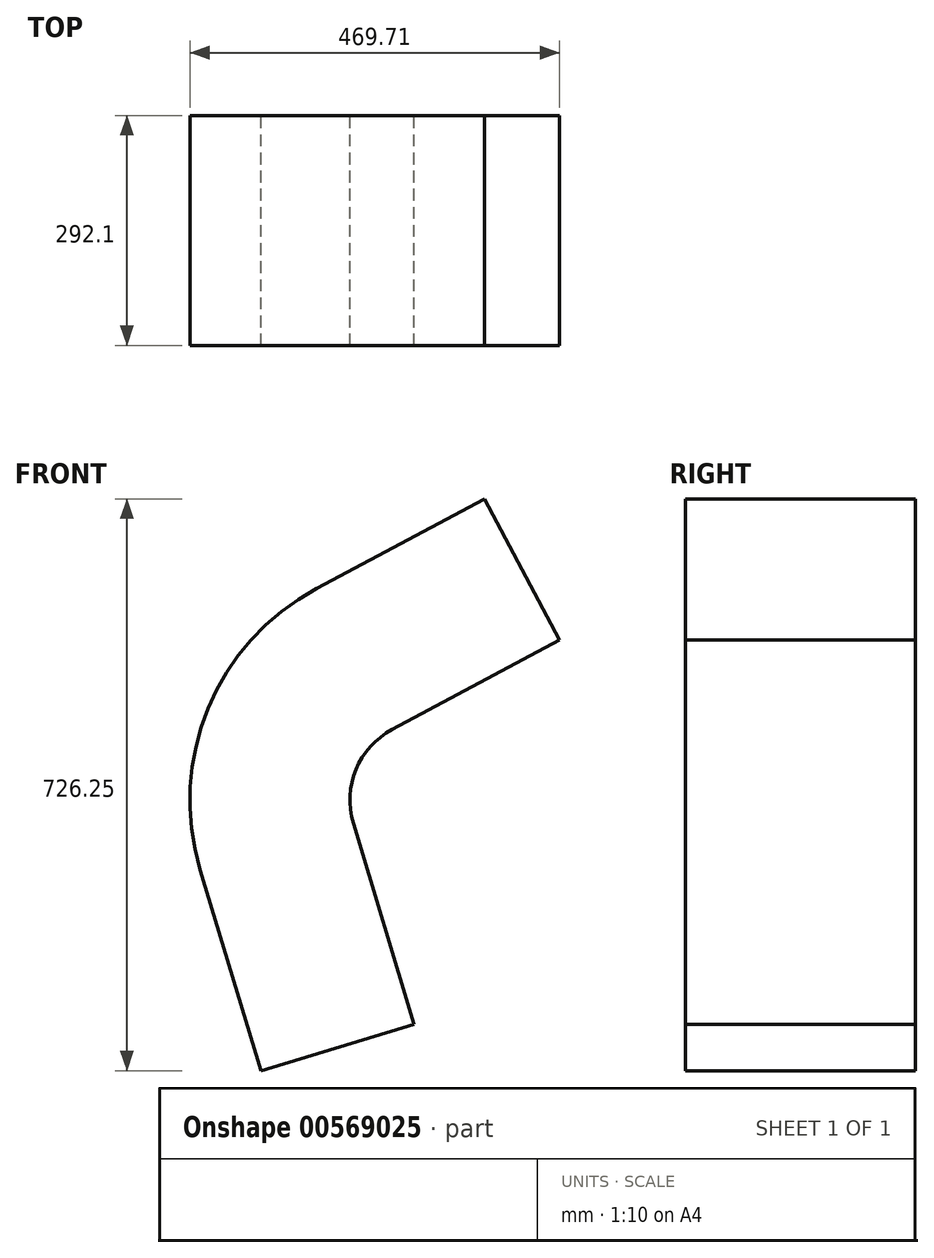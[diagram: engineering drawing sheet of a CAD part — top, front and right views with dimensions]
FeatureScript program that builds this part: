
annotation { "Feature Type Name" : "Feature", "Feature Type Description" : "" }
export const myFeature = defineFeature(function(context is Context, id is Id, definition is map)
    precondition{}
    {
        {
            var Q0;
            Q0=qCreatedBy(makeId("Front.planeOp"),FACE);
            var sketch = newSketch(context, id + "F0", { "sketchPlane" : qUnion([Q0])});
            skCircle(sketch, "E0", {"center": v(0, 0) * mm, "radius": 304.8 * mm});
            skPoint(sketch, "E1.end.orphan", {"position": v(215.53, -215.53) * mm});
            skPoint(sketch, "E2.end.orphan", {"position": v(-215.53, -215.53) * mm});
            skLineSegment(sketch, "E3", {"start": v(0, 0) * mm, "end": v(-281.6, 116.64) * mm});
            skLineSegment(sketch, "E4", {"start": v(0, 0) * mm, "end": v(-298.94, 59.46) * mm});
            skLineSegment(sketch, "E5", {"start": v(0, 0) * mm, "end": v(-291.68, 88.48) * mm});
            skLineSegment(sketch, "E6.MirrorCS", {"start": v(0, 0) * mm, "end": v(-268.8, 143.68) * mm});
            skLineSegment(sketch, "E7.MirrorCS", {"start": v(0, 0) * mm, "end": v(-253.43, 169.34) * mm});
            skLineSegment(sketch, "E8.MirrorCS", {"start": v(0, 0) * mm, "end": v(-235.61, 193.36) * mm});
            skLineSegment(sketch, "E9.MirrorCS", {"start": v(0, 0) * mm, "end": v(-215.53, 215.53) * mm});
            skLineSegment(sketch, "E10.MirrorCS", {"start": v(0, 0) * mm, "end": v(-193.36, 235.61) * mm});
            skLineSegment(sketch, "E11.MirrorCS", {"start": v(0, 0) * mm, "end": v(-169.34, 253.43) * mm});
            skLineSegment(sketch, "E12.MirrorCS", {"start": v(0, 0) * mm, "end": v(-143.68, 268.8) * mm});
            skLineSegment(sketch, "E13.MirrorCS", {"start": v(0, 0) * mm, "end": v(-116.64, 281.6) * mm});
            skLineSegment(sketch, "E14.MirrorCS", {"start": v(0, 0) * mm, "end": v(-88.48, 291.68) * mm});
            skLineSegment(sketch, "E15.MirrorCS", {"start": v(0, 0) * mm, "end": v(-59.46, 298.94) * mm});
            skLineSegment(sketch, "E16.MirrorCS", {"start": v(0, 0) * mm, "end": v(-29.88, 303.33) * mm});
            skLineSegment(sketch, "E17.MirrorCS", {"start": v(0, 0) * mm, "end": v(0, 304.8) * mm});
            skLineSegment(sketch, "E18.MirrorCS", {"start": v(0, 0) * mm, "end": v(29.88, 303.33) * mm});
            skLineSegment(sketch, "E19.MirrorCS", {"start": v(0, 0) * mm, "end": v(59.46, 298.94) * mm});
            skLineSegment(sketch, "E20.MirrorCS", {"start": v(0, 0) * mm, "end": v(88.48, 291.68) * mm});
            skLineSegment(sketch, "E21.MirrorCS", {"start": v(0, 0) * mm, "end": v(116.64, 281.6) * mm});
            skLineSegment(sketch, "E22.MirrorCS", {"start": v(0, 0) * mm, "end": v(143.68, 268.8) * mm});
            skLineSegment(sketch, "E23.MirrorCS", {"start": v(0, 0) * mm, "end": v(169.34, 253.43) * mm});
            skLineSegment(sketch, "E24.MirrorCS", {"start": v(0, 0) * mm, "end": v(193.36, 235.61) * mm});
            skLineSegment(sketch, "E25.MirrorCS", {"start": v(0, 0) * mm, "end": v(215.53, 215.53) * mm});
            skLineSegment(sketch, "E26.MirrorCS", {"start": v(0, 0) * mm, "end": v(235.61, 193.36) * mm});
            skLineSegment(sketch, "E27.MirrorCS", {"start": v(0, 0) * mm, "end": v(253.43, 169.34) * mm});
            skLineSegment(sketch, "E28.MirrorCS", {"start": v(0, 0) * mm, "end": v(268.8, 143.68) * mm});
            skLineSegment(sketch, "E29.MirrorCS", {"start": v(0, 0) * mm, "end": v(281.6, 116.64) * mm});
            skLineSegment(sketch, "E30.MirrorCS", {"start": v(0, 0) * mm, "end": v(291.68, 88.48) * mm});
            skLineSegment(sketch, "E31.MirrorCS", {"start": v(0, 0) * mm, "end": v(298.94, 59.46) * mm});
            skLineSegment(sketch, "E32.MirrorCS", {"start": v(0, 0) * mm, "end": v(303.33, 29.88) * mm});
            skLineSegment(sketch, "E33.MirrorCS", {"start": v(0, 0) * mm, "end": v(304.8, 0) * mm});
            skLineSegment(sketch, "E34.MirrorCS", {"start": v(0, 0) * mm, "end": v(303.33, -29.88) * mm});
            skLineSegment(sketch, "E35.MirrorCS", {"start": v(0, 0) * mm, "end": v(298.94, -59.46) * mm});
            skLineSegment(sketch, "E36.MirrorCS", {"start": v(0, 0) * mm, "end": v(291.68, -88.48) * mm});
            skLineSegment(sketch, "E37.MirrorCS", {"start": v(0, 0) * mm, "end": v(281.6, -116.64) * mm});
            skLineSegment(sketch, "E38.MirrorCS", {"start": v(0, 0) * mm, "end": v(268.8, -143.68) * mm});
            skLineSegment(sketch, "E39.MirrorCS", {"start": v(0, 0) * mm, "end": v(253.43, -169.34) * mm});
            skLineSegment(sketch, "E40.MirrorCS", {"start": v(0, 0) * mm, "end": v(235.61, -193.36) * mm});
            skLineSegment(sketch, "E41.MirrorCS", {"start": v(0, 0) * mm, "end": v(215.53, -215.53) * mm});
            skLineSegment(sketch, "E42.MirrorCS", {"start": v(0, 0) * mm, "end": v(193.36, -235.61) * mm});
            skLineSegment(sketch, "E43.MirrorCS", {"start": v(0, 0) * mm, "end": v(169.34, -253.43) * mm});
            skLineSegment(sketch, "E44.MirrorCS", {"start": v(0, 0) * mm, "end": v(143.68, -268.8) * mm});
            skLineSegment(sketch, "E45.MirrorCS", {"start": v(0, 0) * mm, "end": v(116.64, -281.6) * mm});
            skLineSegment(sketch, "E46.MirrorCS", {"start": v(0, 0) * mm, "end": v(88.48, -291.68) * mm});
            skLineSegment(sketch, "E47.MirrorCS", {"start": v(0, 0) * mm, "end": v(59.46, -298.94) * mm});
            skLineSegment(sketch, "E48.MirrorCS", {"start": v(0, 0) * mm, "end": v(29.88, -303.33) * mm});
            skLineSegment(sketch, "E49.MirrorCS", {"start": v(0, 0) * mm, "end": v(0, -304.8) * mm});
            skLineSegment(sketch, "E50.MirrorCS", {"start": v(0, 0) * mm, "end": v(-29.88, -303.33) * mm});
            skLineSegment(sketch, "E51.MirrorCS", {"start": v(0, 0) * mm, "end": v(-59.46, -298.94) * mm});
            skLineSegment(sketch, "E52.MirrorCS", {"start": v(0, 0) * mm, "end": v(-88.48, -291.68) * mm});
            skLineSegment(sketch, "E53.MirrorCS", {"start": v(0, 0) * mm, "end": v(-116.64, -281.6) * mm});
            skLineSegment(sketch, "E54.MirrorCS", {"start": v(0, 0) * mm, "end": v(-143.68, -268.8) * mm});
            skLineSegment(sketch, "E55.MirrorCS", {"start": v(0, 0) * mm, "end": v(-169.34, -253.43) * mm});
            skLineSegment(sketch, "E56.MirrorCS", {"start": v(0, 0) * mm, "end": v(-193.36, -235.61) * mm});
            skLineSegment(sketch, "E57.MirrorCS", {"start": v(0, 0) * mm, "end": v(-215.53, -215.53) * mm});
            skLineSegment(sketch, "E58.MirrorCS", {"start": v(0, 0) * mm, "end": v(-235.61, -193.36) * mm});
            skLineSegment(sketch, "E59.MirrorCS", {"start": v(0, 0) * mm, "end": v(-253.43, -169.34) * mm});
            skLineSegment(sketch, "E60.MirrorCS", {"start": v(0, 0) * mm, "end": v(-268.8, -143.68) * mm});
            skLineSegment(sketch, "E61.MirrorCS", {"start": v(0, 0) * mm, "end": v(-281.6, -116.64) * mm});
            skLineSegment(sketch, "E62.MirrorCS", {"start": v(0, 0) * mm, "end": v(-291.68, -88.48) * mm});
            skLineSegment(sketch, "E63.MirrorCS", {"start": v(0, 0) * mm, "end": v(-303.33, -29.88) * mm});
            skLineSegment(sketch, "E64.MirrorCS", {"start": v(0, 0) * mm, "end": v(-298.94, -59.46) * mm});
            skLineSegment(sketch, "E65.MirrorCS", {"start": v(0, 0) * mm, "end": v(-304.8, 0) * mm});
            skLineSegment(sketch, "E66.MirrorCS", {"start": v(0, 0) * mm, "end": v(-303.33, 29.88) * mm});
            skCircle(sketch, "E67", {"center": v(0, 0) * mm, "radius": 317.5 * mm});
            skCircle(sketch, "E68", {"center": v(0, 0) * mm, "radius": 101.6 * mm});
            skSolve(sketch);
        }
        {
            var Q0;
            {var subQ0=sQuery(id+"F0.wireOp",EDGE,"E12.MirrorCS");var subQ1=sQuery(id+"F0.wireOp",EDGE,"E0");var subQ2=makeQuery(id+"F0.imprint","INTERSECT",VERTEX,{"derivedFrom":[subQ1,subQ0]});Q0=makeQuery(id+"F0.imprint","IMPRINT",FACE,{"disambiguationData":[TD([[makeQuery(id+"F0.imprint","IMPRINT",EDGE,{"disambiguationData":[TD([[subQ2,-1.0]])],"derivedFrom":subQ1}),1.0]])]});}
            var Q1;
            {var subQ0=sQuery(id+"F0.wireOp",EDGE,"E66.MirrorCS");var subQ1=sQuery(id+"F0.wireOp",EDGE,"E0");var subQ2=makeQuery(id+"F0.imprint","INTERSECT",VERTEX,{"derivedFrom":[subQ1,subQ0]});Q1=makeQuery(id+"F0.imprint","IMPRINT",FACE,{"disambiguationData":[TD([[makeQuery(id+"F0.imprint","IMPRINT",EDGE,{"disambiguationData":[TD([[subQ2,-1.0]])],"derivedFrom":subQ1}),1.0]])]});}
            var Q2;
            {var subQ0=sQuery(id+"F0.wireOp",EDGE,"E4");var subQ1=sQuery(id+"F0.wireOp",EDGE,"E0");var subQ2=makeQuery(id+"F0.imprint","INTERSECT",VERTEX,{"derivedFrom":[subQ1,subQ0]});Q2=makeQuery(id+"F0.imprint","IMPRINT",FACE,{"disambiguationData":[TD([[makeQuery(id+"F0.imprint","IMPRINT",EDGE,{"disambiguationData":[TD([[subQ2,-1.0]])],"derivedFrom":subQ1}),1.0]])]});}
            var Q3;
            {var subQ0=sQuery(id+"F0.wireOp",EDGE,"E11.MirrorCS");var subQ1=sQuery(id+"F0.wireOp",EDGE,"E0");var subQ2=makeQuery(id+"F0.imprint","INTERSECT",VERTEX,{"derivedFrom":[subQ1,subQ0]});Q3=makeQuery(id+"F0.imprint","IMPRINT",FACE,{"disambiguationData":[TD([[makeQuery(id+"F0.imprint","IMPRINT",EDGE,{"disambiguationData":[TD([[subQ2,-1.0]])],"derivedFrom":subQ1}),1.0]])]});}
            var Q4;
            {var subQ0=sQuery(id+"F0.wireOp",EDGE,"E65.MirrorCS");var subQ1=sQuery(id+"F0.wireOp",EDGE,"E0");var subQ2=makeQuery(id+"F0.imprint","INTERSECT",VERTEX,{"derivedFrom":[subQ1,subQ0]});Q4=makeQuery(id+"F0.imprint","IMPRINT",FACE,{"disambiguationData":[TD([[makeQuery(id+"F0.imprint","IMPRINT",EDGE,{"disambiguationData":[TD([[subQ2,-1.0]])],"derivedFrom":subQ1}),1.0]])]});}
            var Q5;
            {var subQ0=sQuery(id+"F0.wireOp",EDGE,"E10.MirrorCS");var subQ1=sQuery(id+"F0.wireOp",EDGE,"E0");var subQ2=makeQuery(id+"F0.imprint","INTERSECT",VERTEX,{"derivedFrom":[subQ1,subQ0]});Q5=makeQuery(id+"F0.imprint","IMPRINT",FACE,{"disambiguationData":[TD([[makeQuery(id+"F0.imprint","IMPRINT",EDGE,{"disambiguationData":[TD([[subQ2,-1.0]])],"derivedFrom":subQ1}),1.0]])]});}
            var Q6;
            {var subQ0=sQuery(id+"F0.wireOp",EDGE,"E63.MirrorCS");var subQ1=sQuery(id+"F0.wireOp",EDGE,"E0");var subQ2=makeQuery(id+"F0.imprint","INTERSECT",VERTEX,{"derivedFrom":[subQ1,subQ0]});Q6=makeQuery(id+"F0.imprint","IMPRINT",FACE,{"disambiguationData":[TD([[makeQuery(id+"F0.imprint","IMPRINT",EDGE,{"disambiguationData":[TD([[subQ2,-1.0]])],"derivedFrom":subQ1}),1.0]])]});}
            var Q7;
            {var subQ0=sQuery(id+"F0.wireOp",EDGE,"E9.MirrorCS");var subQ1=sQuery(id+"F0.wireOp",EDGE,"E0");var subQ2=makeQuery(id+"F0.imprint","INTERSECT",VERTEX,{"derivedFrom":[subQ1,subQ0]});Q7=makeQuery(id+"F0.imprint","IMPRINT",FACE,{"disambiguationData":[TD([[makeQuery(id+"F0.imprint","IMPRINT",EDGE,{"disambiguationData":[TD([[subQ2,-1.0]])],"derivedFrom":subQ1}),1.0]])]});}
            var Q8;
            {var subQ0=sQuery(id+"F0.wireOp",EDGE,"E64.MirrorCS");var subQ1=sQuery(id+"F0.wireOp",EDGE,"E0");var subQ2=makeQuery(id+"F0.imprint","INTERSECT",VERTEX,{"derivedFrom":[subQ1,subQ0]});Q8=makeQuery(id+"F0.imprint","IMPRINT",FACE,{"disambiguationData":[TD([[makeQuery(id+"F0.imprint","IMPRINT",EDGE,{"disambiguationData":[TD([[subQ2,-1.0]])],"derivedFrom":subQ1}),1.0]])]});}
            var Q9;
            {var subQ0=sQuery(id+"F0.wireOp",EDGE,"E7.MirrorCS");var subQ1=sQuery(id+"F0.wireOp",EDGE,"E0");var subQ2=makeQuery(id+"F0.imprint","INTERSECT",VERTEX,{"derivedFrom":[subQ1,subQ0]});Q9=makeQuery(id+"F0.imprint","IMPRINT",FACE,{"disambiguationData":[TD([[makeQuery(id+"F0.imprint","IMPRINT",EDGE,{"disambiguationData":[TD([[subQ2,-1.0]])],"derivedFrom":subQ1}),1.0]])]});}
            var Q10;
            {var subQ0=sQuery(id+"F0.wireOp",EDGE,"E6.MirrorCS");var subQ1=sQuery(id+"F0.wireOp",EDGE,"E0");var subQ2=makeQuery(id+"F0.imprint","INTERSECT",VERTEX,{"derivedFrom":[subQ1,subQ0]});Q10=makeQuery(id+"F0.imprint","IMPRINT",FACE,{"disambiguationData":[TD([[makeQuery(id+"F0.imprint","IMPRINT",EDGE,{"disambiguationData":[TD([[subQ2,-1.0]])],"derivedFrom":subQ1}),1.0]])]});}
            var Q11;
            {var subQ0=sQuery(id+"F0.wireOp",EDGE,"E3");var subQ1=sQuery(id+"F0.wireOp",EDGE,"E0");var subQ2=makeQuery(id+"F0.imprint","INTERSECT",VERTEX,{"derivedFrom":[subQ1,subQ0]});Q11=makeQuery(id+"F0.imprint","IMPRINT",FACE,{"disambiguationData":[TD([[makeQuery(id+"F0.imprint","IMPRINT",EDGE,{"disambiguationData":[TD([[subQ2,-1.0]])],"derivedFrom":subQ1}),1.0]])]});}
            var Q12;
            {var subQ0=sQuery(id+"F0.wireOp",EDGE,"E8.MirrorCS");var subQ1=sQuery(id+"F0.wireOp",EDGE,"E0");var subQ2=makeQuery(id+"F0.imprint","INTERSECT",VERTEX,{"derivedFrom":[subQ1,subQ0]});Q12=makeQuery(id+"F0.imprint","IMPRINT",FACE,{"disambiguationData":[TD([[makeQuery(id+"F0.imprint","IMPRINT",EDGE,{"disambiguationData":[TD([[subQ2,-1.0]])],"derivedFrom":subQ1}),1.0]])]});}
            var Q13;
            {var subQ0=sQuery(id+"F0.wireOp",EDGE,"E5");var subQ1=sQuery(id+"F0.wireOp",EDGE,"E0");var subQ2=makeQuery(id+"F0.imprint","INTERSECT",VERTEX,{"derivedFrom":[subQ1,subQ0]});Q13=makeQuery(id+"F0.imprint","IMPRINT",FACE,{"disambiguationData":[TD([[makeQuery(id+"F0.imprint","IMPRINT",EDGE,{"disambiguationData":[TD([[subQ2,-1.0]])],"derivedFrom":subQ1}),1.0]])]});}
            extrude(context, id + "F1", {"entities" : qUnion([Q0, Q1, Q2, Q3, Q4, Q5, Q6, Q7, Q8, Q9, Q10, Q11, Q12, Q13]), "depth" : 292.1 * mm, "offsetDistance" : 25.4 * mm});
        }
        {
            var Q0;
            Q0=qCreatedBy(makeId("Front.planeOp"),FACE);
            var sketch = newSketch(context, id + "F2", { "sketchPlane" : qUnion([Q0])});
            skSolve(sketch);
        }
        {
            var Q0;
            Q0 = qSketchRegion(id + "F2", true);
            var Q1;
            Q1=makeQuery(id+"F1.opExtrude","SWEPT_FACE",FACE,{"disambiguationData":[OSD([sQuery(id+"F0.wireOp",EDGE,"E12.MirrorCS")])]});
            extrude(context, id + "F3", {"entities" : qUnion([Q0, Q1]), "operationType" : NewBodyOperationType.ADD, "depth" : 241.3 * mm, "offsetDistance" : 25.4 * mm});
        }
        {
            var Q0;
            Q0=makeQuery(id+"F1.opExtrude","SWEPT_FACE",FACE,{"disambiguationData":[OSD([sQuery(id+"F0.wireOp",EDGE,"E62.MirrorCS")])]});
            var sketch = newSketch(context, id + "F4", { "sketchPlane" : qUnion([Q0])});
            skSolve(sketch);
        }
        {
            var Q0;
            {var subQ0=sQuery(id+"F0.wireOp",EDGE,"E62.MirrorCS");Q0=makeQuery(id+"F4.imprint","IMPRINT",FACE,{"disambiguationData":[TD([[makeQuery(id+"F4.imprint","IMPRINT",EDGE,{"derivedFrom":makeQuery(id+"F1.opExtrude","CAP_EDGE",EDGE,{"disambiguationData":[OSD([subQ0])],"isStart":true})}),-1.0]])]});}
            extrude(context, id + "F5", {"entities" : qUnion([Q0]), "operationType" : NewBodyOperationType.ADD, "depth" : 266.7 * mm, "offsetDistance" : 25.4 * mm});
        }
    });
